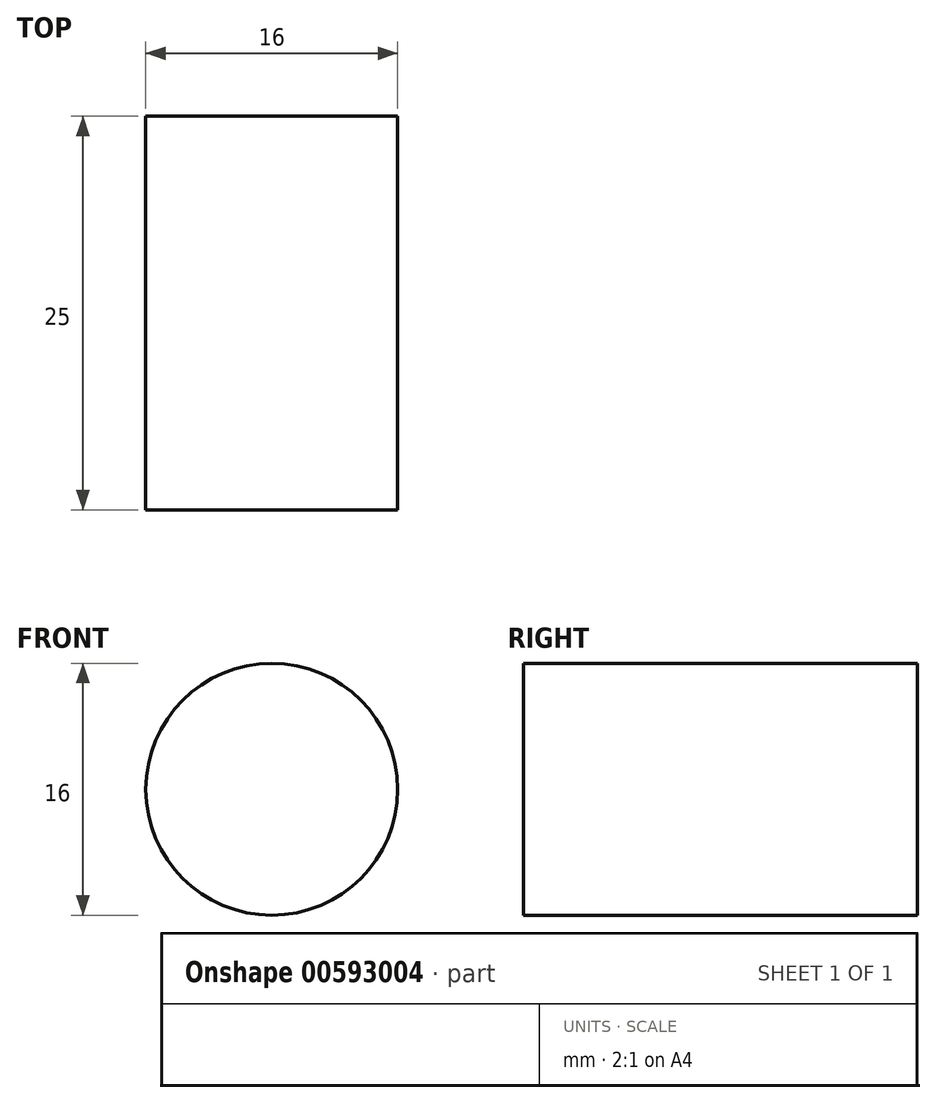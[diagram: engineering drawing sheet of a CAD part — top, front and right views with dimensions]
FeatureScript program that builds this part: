
annotation { "Feature Type Name" : "Feature", "Feature Type Description" : "" }
export const myFeature = defineFeature(function(context is Context, id is Id, definition is map)
    precondition{}
    {
        {
            var Q0;
            Q0=qCreatedBy(makeId("Front.planeOp"),FACE);
            var sketch = newSketch(context, id + "F0", { "sketchPlane" : qUnion([Q0])});
            skCircle(sketch, "E0", {"center": v(0, 0) * mm, "radius": 8 * mm});
            skSolve(sketch);
        }
        {
            var Q0;
            Q0=makeQuery(id+"F0.imprint","IMPRINT",FACE,{"disambiguationData":[TD([[makeQuery(id+"F0.imprint","IMPRINT",EDGE,{"derivedFrom":sQuery(id+"F0.wireOp",EDGE,"E0")}),1.0]])]});
            var Q1;
            Q1=sQuery(id+"F0.wireOp",EDGE,"E0");
            extrude(context, id + "F1", {"entities" : qUnion([Q0]), "surfaceEntities" : qUnion([Q1]), "depth" : 25 * mm, "offsetDistance" : 25 * mm});
        }
    });
